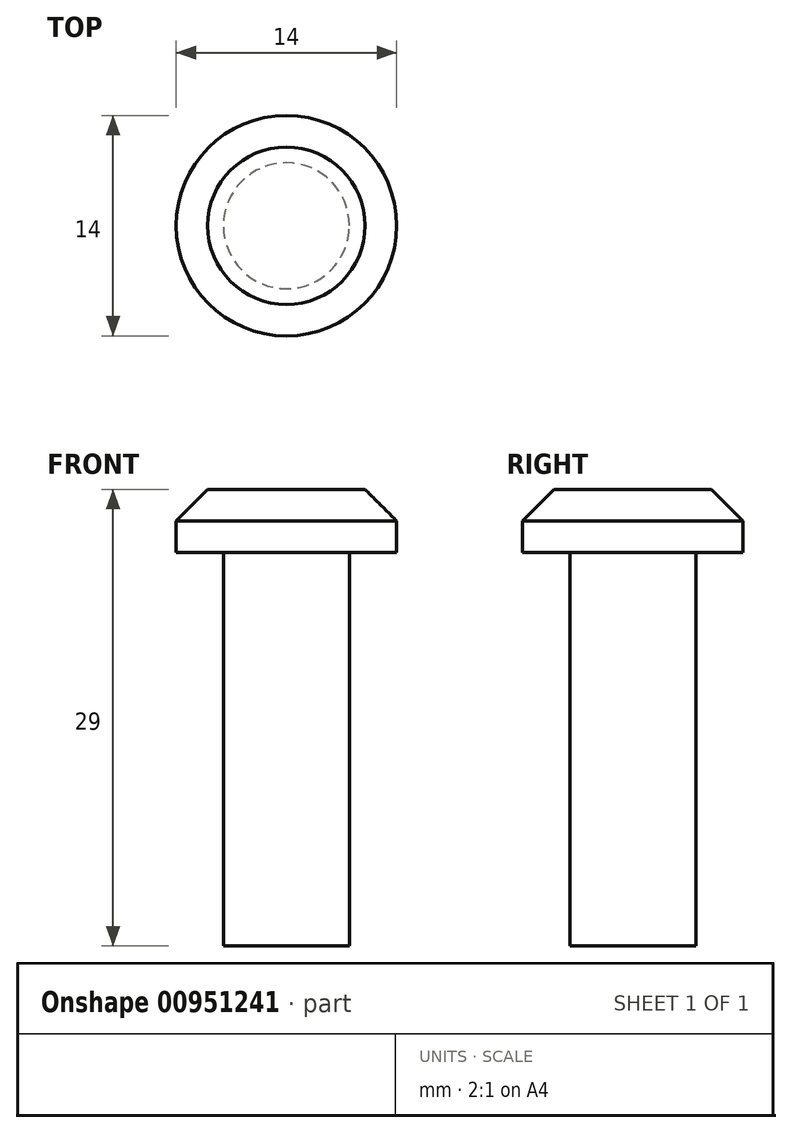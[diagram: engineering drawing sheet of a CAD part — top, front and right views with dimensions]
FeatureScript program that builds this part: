
annotation { "Feature Type Name" : "Feature", "Feature Type Description" : "" }
export const myFeature = defineFeature(function(context is Context, id is Id, definition is map)
    precondition{}
    {
        {
            var Q0;
            Q0=qCreatedBy(makeId("Front.planeOp"),FACE);
            var sketch = newSketch(context, id + "F0", { "sketchPlane" : qUnion([Q0])});
            skLineSegment(sketch, "E0", {"start": v(0, 0) * mm, "end": v(4, 0) * mm});
            skLineSegment(sketch, "E1", {"start": v(4, 0) * mm, "end": v(4, 25) * mm});
            skLineSegment(sketch, "E2", {"start": v(4, 25) * mm, "end": v(7, 25) * mm});
            skLineSegment(sketch, "E3", {"start": v(7, 25) * mm, "end": v(7, 29) * mm});
            skLineSegment(sketch, "E4", {"start": v(7, 29) * mm, "end": v(0, 29) * mm});
            skLineSegment(sketch, "E5", {"start": v(0, 29) * mm, "end": v(0, 0) * mm});
            skLineSegment(sketch, "E6", {"start": v(0, 0) * mm, "end": v(0, 35) * mm, "construction": true});
            skSolve(sketch);
        }
        {
            var Q0;
            Q0=makeQuery(id+"F0.imprint","IMPRINT",FACE,{"disambiguationData":[TD([[makeQuery(id+"F0.imprint","IMPRINT",EDGE,{"derivedFrom":sQuery(id+"F0.wireOp",EDGE,"E0")}),1.0]])]});
            var Q1;
            Q1=sQuery(id+"F0.wireOp",EDGE,"E6");
            revolve(context, id + "F1", {"surfaceOperationType" : NewSurfaceOperationType.NEW, "entities" : qUnion([Q0]), "axis" : qUnion([Q1]), "revolveType" : RevolveType.FULL});
        }
        {
            var Q0;
            Q0=makeQuery(id+"F1.opRevolve","SWEPT_EDGE",EDGE,{"disambiguationData":[OSD([sQuery(id+"F0.wireOp",EDGE,"E3"),sQuery(id+"F0.wireOp",EDGE,"E4")])]});
            chamfer(context, id + "F2", {"entities" : qUnion([Q0]), "width" : 2 * mm, "tangentPropagation" : true});
        }
    });
